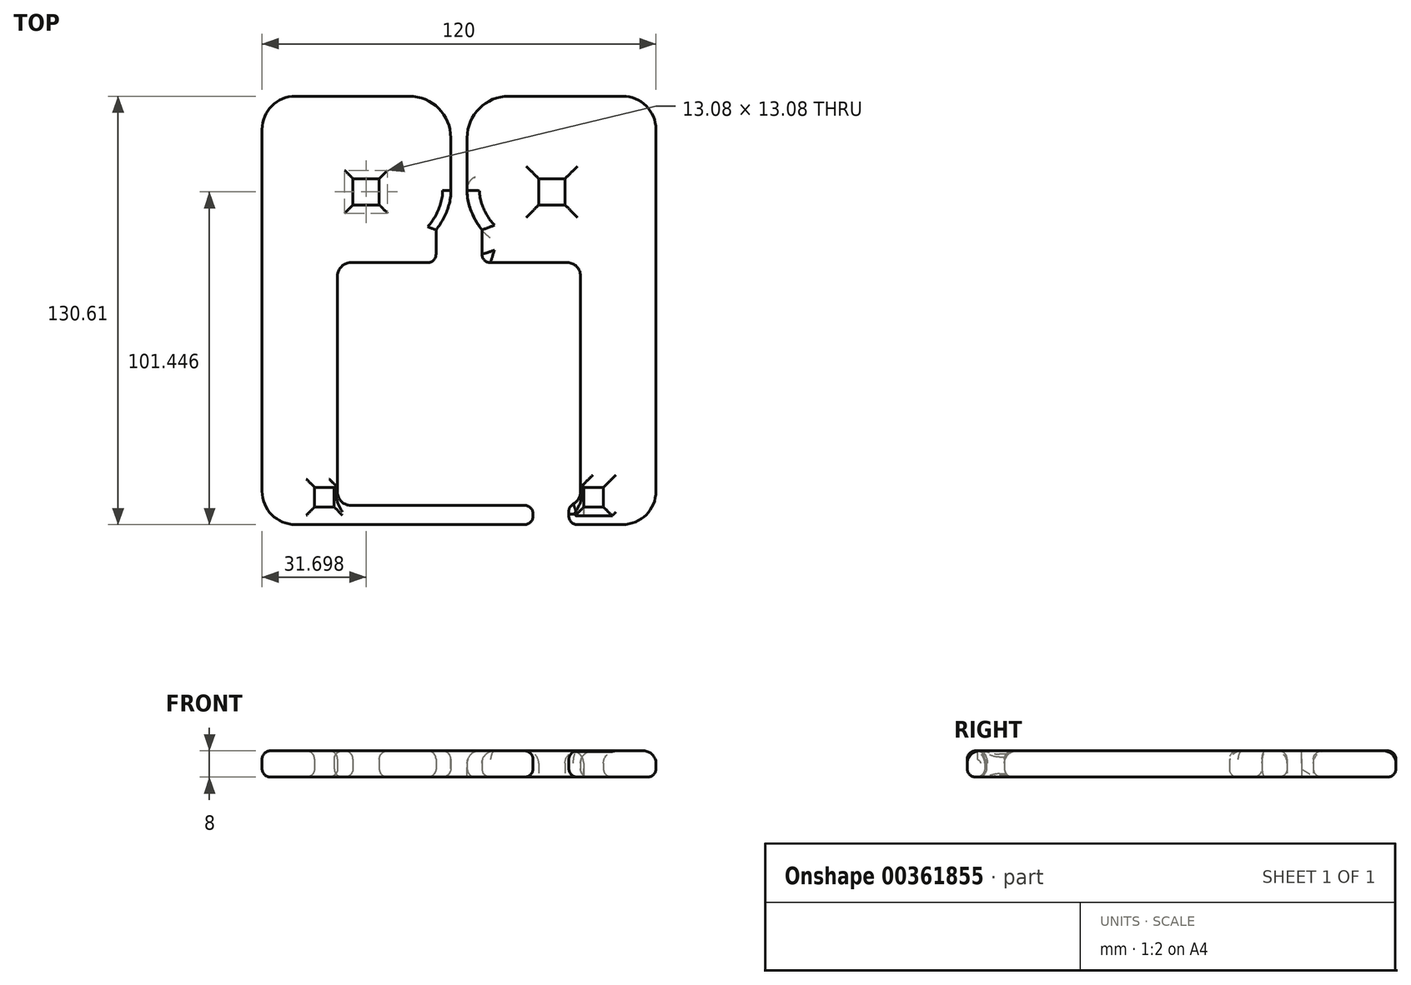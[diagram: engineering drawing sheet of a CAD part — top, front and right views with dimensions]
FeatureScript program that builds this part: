
annotation { "Feature Type Name" : "Feature", "Feature Type Description" : "" }
export const myFeature = defineFeature(function(context is Context, id is Id, definition is map)
    precondition{}
    {
        {
            var Q0;
            Q0=qCreatedBy(makeId("Top.planeOp"),FACE);
            var sketch = newSketch(context, id + "F0", { "sketchPlane" : qUnion([Q0])});
            skLineSegment(sketch, "E0.2", {"start": v(-99.34, -42.29) * mm, "end": v(-99.34, 23.71) * mm});
            skArc(sketch, "E0.3", {"start": v(-112.18, 78.48) * mm, "mid": v(-119.37, 75.5) * mm, "end": v(-122.34, 68.32) * mm});
            skLineSegment(sketch, "E0.5", {"start": v(-95.34, 23.71) * mm, "end": v(-99.34, 23.71) * mm});
            skLineSegment(sketch, "E1.0.0", {"start": v(-122.34, 68.32) * mm, "end": v(-122.34, -41.97) * mm});
            skLineSegment(sketch, "E1.0.4", {"start": v(-2.34, -41.97) * mm, "end": v(-2.34, 68.32) * mm});
            skArc(sketch, "E1.0.5", {"start": v(-2.34, 68.32) * mm, "mid": v(-5.32, 75.5) * mm, "end": v(-12.5, 78.48) * mm});
            skLineSegment(sketch, "E1.0.6", {"start": v(-12.5, 78.48) * mm, "end": v(-47.14, 78.48) * mm});
            skLineSegment(sketch, "E2.0.0", {"start": v(-28.87, -46.26) * mm, "end": v(-28.87, -52.13) * mm});
            skLineSegment(sketch, "E2.0.11", {"start": v(-39.8, -52.13) * mm, "end": v(-39.8, -46.29) * mm});
            skLineSegment(sketch, "E2.0.12", {"start": v(-39.8, -46.29) * mm, "end": v(-95.34, -46.29) * mm});
            skArc(sketch, "E2.0.13", {"start": v(-95.34, -46.29) * mm, "mid": v(-98.17, -45.12) * mm, "end": v(-99.34, -42.29) * mm});
            skArc(sketch, "E2.0.15", {"start": v(-99.34, 23.71) * mm, "mid": v(-98.17, 26.54) * mm, "end": v(-95.34, 27.71) * mm});
            skLineSegment(sketch, "E2.0.16", {"start": v(-95.34, 27.71) * mm, "end": v(-69.34, 27.71) * mm});
            skArc(sketch, "E2.0.17", {"start": v(-29.34, 27.71) * mm, "mid": v(-26.51, 26.54) * mm, "end": v(-25.34, 23.71) * mm});
            skLineSegment(sketch, "E2.0.18", {"start": v(-25.34, 23.71) * mm, "end": v(-25.34, -42.29) * mm});
            skArc(sketch, "E2.0.19", {"start": v(-25.34, -42.29) * mm, "mid": v(-26.35, -44.95) * mm, "end": v(-28.87, -46.26) * mm});
            skLineSegment(sketch, "E3.0.0", {"start": v(-94.64, 53.32) * mm, "end": v(-94.64, 45.32) * mm});
            skLineSegment(sketch, "E3.0.1", {"start": v(-94.64, 45.32) * mm, "end": v(-86.64, 45.32) * mm});
            skLineSegment(sketch, "E3.0.2", {"start": v(-86.64, 45.32) * mm, "end": v(-86.64, 53.32) * mm});
            skLineSegment(sketch, "E3.0.3", {"start": v(-86.64, 53.32) * mm, "end": v(-94.64, 53.32) * mm});
            skLineSegment(sketch, "E4.0.0", {"start": v(-30.04, 45.32) * mm, "end": v(-30.04, 53.32) * mm});
            skLineSegment(sketch, "E4.0.1", {"start": v(-30.04, 53.32) * mm, "end": v(-38.04, 53.32) * mm});
            skLineSegment(sketch, "E4.0.2", {"start": v(-38.04, 53.32) * mm, "end": v(-38.04, 45.32) * mm});
            skLineSegment(sketch, "E4.0.3", {"start": v(-38.04, 45.32) * mm, "end": v(-30.04, 45.32) * mm});
            skLineSegment(sketch, "E5", {"start": v(-105.84, -43.79) * mm, "end": v(-106.34, -43.79) * mm, "construction": true});
            skLineSegment(sketch, "E6", {"start": v(-103.34, -41.29) * mm, "end": v(-103.34, -40.79) * mm, "construction": true});
            skLineSegment(sketch, "E7.bottom", {"start": v(-106.34, -40.79) * mm, "end": v(-100.34, -40.79) * mm});
            skLineSegment(sketch, "E7.top", {"start": v(-106.34, -46.79) * mm, "end": v(-100.34, -46.79) * mm});
            skLineSegment(sketch, "E7.left", {"start": v(-106.34, -40.79) * mm, "end": v(-106.34, -46.79) * mm});
            skLineSegment(sketch, "E7.right", {"start": v(-100.34, -40.79) * mm, "end": v(-100.34, -46.79) * mm});
            skLineSegment(sketch, "E8", {"start": v(-99.34, -9.29) * mm, "end": v(-25.34, -9.29) * mm, "construction": true});
            skLineSegment(sketch, "E9", {"start": v(-62.34, -3.3) * mm, "end": v(-62.34, -18.16) * mm, "construction": true});
            skPoint(sketch, "E9.startSnap0", {"position": v(-62.34, -9.29) * mm});
            skLineSegment(sketch, "E10.MirrorCS", {"start": v(-21.34, -41.29) * mm, "end": v(-21.34, -40.79) * mm, "construction": true});
            skLineSegment(sketch, "E11.MirrorCS", {"start": v(-24.34, -40.79) * mm, "end": v(-24.34, -46.79) * mm});
            skLineSegment(sketch, "E12.MirrorCS", {"start": v(-18.34, -40.79) * mm, "end": v(-18.34, -46.79) * mm});
            skLineSegment(sketch, "E13.MirrorCS", {"start": v(-18.34, -40.79) * mm, "end": v(-24.34, -40.79) * mm});
            skLineSegment(sketch, "E14.MirrorCS", {"start": v(-18.34, -46.79) * mm, "end": v(-24.34, -46.79) * mm});
            skLineSegment(sketch, "E15", {"start": v(-99.34, -3.05) * mm, "end": v(-69.34, -3.05) * mm, "construction": true});
            skLineSegment(sketch, "E16", {"start": v(-25.34, -3.05) * mm, "end": v(-55.34, -3.05) * mm, "construction": true});
            skLineSegment(sketch, "E17", {"start": v(-69.34, -3.05) * mm, "end": v(-69.34, 27.71) * mm, "construction": true});
            skLineSegment(sketch, "E18", {"start": v(-55.34, 27.71) * mm, "end": v(-55.34, -3.05) * mm, "construction": true});
            skLineSegment(sketch, "E19.trimOffspring", {"start": v(-55.34, 27.71) * mm, "end": v(-29.34, 27.71) * mm});
            skLineSegment(sketch, "E20", {"start": v(-69.34, 27.71) * mm, "end": v(-69.34, 37.71) * mm});
            skLineSegment(sketch, "E21", {"start": v(-55.34, 27.71) * mm, "end": v(-55.34, 37.71) * mm});
            skLineSegment(sketch, "E22", {"start": v(-64.84, 48.63) * mm, "end": v(-64.84, 65.78) * mm});
            skLineSegment(sketch, "E23", {"start": v(-59.84, 48.63) * mm, "end": v(-59.84, 65.78) * mm});
            skEllipticalArc(sketch, "E24", {});
            skEllipticalArc(sketch, "E25.MirrorC", {});
            skLineSegment(sketch, "E26.trimOffspring", {"start": v(-77.54, 78.48) * mm, "end": v(-112.18, 78.48) * mm});
            skPoint(sketch, "E27.visualSharp", {"position": v(-64.84, 78.48) * mm});
            skArc(sketch, "E27.filletArc", {"start": v(-64.84, 65.78) * mm, "mid": v(-68.56, 74.76) * mm, "end": v(-77.54, 78.48) * mm});
            skPoint(sketch, "E28.visualSharp", {"position": v(-59.84, 78.48) * mm});
            skArc(sketch, "E28.filletArc", {"start": v(-47.14, 78.48) * mm, "mid": v(-56.12, 74.76) * mm, "end": v(-59.84, 65.78) * mm});
            skLineSegment(sketch, "E29", {"start": v(-112.18, -52.13) * mm, "end": v(-39.8, -52.13) * mm});
            skPoint(sketch, "E30.visualSharp", {"position": v(-2.34, -52.13) * mm});
            skArc(sketch, "E30.filletArc", {"start": v(-12.5, -52.13) * mm, "mid": v(-5.32, -49.16) * mm, "end": v(-2.34, -41.97) * mm});
            skPoint(sketch, "E31.visualSharp", {"position": v(-122.34, -52.13) * mm});
            skArc(sketch, "E31.filletArc", {"start": v(-122.34, -41.97) * mm, "mid": v(-119.37, -49.16) * mm, "end": v(-112.18, -52.13) * mm});
            skLineSegment(sketch, "E32.trimOffspring", {"start": v(-28.87, -52.13) * mm, "end": v(-12.5, -52.13) * mm});
            const initialGuessF0  = {"E24": [-0.07160861045122147, 0.04385959729552269, -0.4506115327281223, -0.8927201389978903, 0.010858769683543398, 0.005259403551116595, 1.146709446237365, 2.4446029381637704], "E25.MirrorC": [-0.053077005265114885, 0.04385959729552269, 0.4506115327281223, -0.8927201389978903, 0.010858769683543398, 0.005259403551116595, 3.838582369015851, 5.1364758609422205]};
            skSetInitialGuess(sketch, initialGuessF0);
            skSolve(sketch);
        }
        {
            var Q0;
            Q0 = qSketchRegion(id + "F0", true);
            extrude(context, id + "F1", {"entities" : qUnion([Q0]), "depth" : 8 * mm});
        }
        {
            var Q0;
            Q0=makeQuery(id+"F1.opExtrude","SWEPT_EDGE",EDGE,{"disambiguationData":[OSD([sQuery(id+"F0.wireOp",EDGE,"E2.0.11"),sQuery(id+"F0.wireOp",EDGE,"E29")])]});
            var Q1;
            Q1=makeQuery(id+"F1.opExtrude","SWEPT_EDGE",EDGE,{"disambiguationData":[OSD([sQuery(id+"F0.wireOp",EDGE,"E2.0.11"),sQuery(id+"F0.wireOp",EDGE,"E2.0.12")])]});
            var Q2;
            Q2=makeQuery(id+"F1.opExtrude","SWEPT_EDGE",EDGE,{"disambiguationData":[OSD([sQuery(id+"F0.wireOp",EDGE,"E2.0.16"),sQuery(id+"F0.wireOp",EDGE,"E20")])]});
            var Q3;
            Q3=makeQuery(id+"F1.opExtrude","SWEPT_EDGE",EDGE,{"disambiguationData":[OSD([sQuery(id+"F0.wireOp",EDGE,"E19.trimOffspring"),sQuery(id+"F0.wireOp",EDGE,"E21")])]});
            fillet(context, id + "F2", {"entities" : qUnion([Q0, Q1, Q2, Q3]), "radius" : 2.54 * mm, "tangentPropagation" : true, "allowEdgeOverflow" : false});
        }
        {
            var Q0;
            Q0=makeQuery(id+"F1.opExtrude","CAP_EDGE",EDGE,{"disambiguationData":[OSD([sQuery(id+"F0.wireOp",EDGE,"E27.filletArc")])],"isStart":true});
            var Q1;
            Q1=makeQuery(id+"F1.opExtrude","CAP_FACE",FACE,{"disambiguationData":[OSD([sQuery(id+"F0.wireOp",EDGE,"E1.0.0"),sQuery(id+"F0.wireOp",EDGE,"E0.3"),sQuery(id+"F0.wireOp",EDGE,"E2.0.11"),sQuery(id+"F0.wireOp",EDGE,"E2.0.12"),sQuery(id+"F0.wireOp",EDGE,"E2.0.13"),sQuery(id+"F0.wireOp",EDGE,"E0.2"),sQuery(id+"F0.wireOp",EDGE,"E2.0.15"),sQuery(id+"F0.wireOp",EDGE,"E2.0.16"),sQuery(id+"F0.wireOp",EDGE,"E3.0.0"),sQuery(id+"F0.wireOp",EDGE,"E3.0.1"),sQuery(id+"F0.wireOp",EDGE,"E3.0.2"),sQuery(id+"F0.wireOp",EDGE,"E3.0.3"),sQuery(id+"F0.wireOp",EDGE,"E7.bottom"),sQuery(id+"F0.wireOp",EDGE,"E7.top"),sQuery(id+"F0.wireOp",EDGE,"E7.left"),sQuery(id+"F0.wireOp",EDGE,"E7.right"),sQuery(id+"F0.wireOp",EDGE,"E20"),sQuery(id+"F0.wireOp",EDGE,"E22"),sQuery(id+"F0.wireOp",EDGE,"E24"),sQuery(id+"F0.wireOp",EDGE,"E26.trimOffspring"),sQuery(id+"F0.wireOp",EDGE,"E27.filletArc"),sQuery(id+"F0.wireOp",EDGE,"E29"),sQuery(id+"F0.wireOp",EDGE,"E31.filletArc")])],"isStart":true});
            var Q2;
            Q2=makeQuery(id+"F1.opExtrude","CAP_FACE",FACE,{"disambiguationData":[OSD([sQuery(id+"F0.wireOp",EDGE,"E1.0.0"),sQuery(id+"F0.wireOp",EDGE,"E0.3"),sQuery(id+"F0.wireOp",EDGE,"E2.0.11"),sQuery(id+"F0.wireOp",EDGE,"E2.0.12"),sQuery(id+"F0.wireOp",EDGE,"E2.0.13"),sQuery(id+"F0.wireOp",EDGE,"E0.2"),sQuery(id+"F0.wireOp",EDGE,"E2.0.15"),sQuery(id+"F0.wireOp",EDGE,"E2.0.16"),sQuery(id+"F0.wireOp",EDGE,"E3.0.0"),sQuery(id+"F0.wireOp",EDGE,"E3.0.1"),sQuery(id+"F0.wireOp",EDGE,"E3.0.2"),sQuery(id+"F0.wireOp",EDGE,"E3.0.3"),sQuery(id+"F0.wireOp",EDGE,"E7.bottom"),sQuery(id+"F0.wireOp",EDGE,"E7.top"),sQuery(id+"F0.wireOp",EDGE,"E7.left"),sQuery(id+"F0.wireOp",EDGE,"E7.right"),sQuery(id+"F0.wireOp",EDGE,"E20"),sQuery(id+"F0.wireOp",EDGE,"E22"),sQuery(id+"F0.wireOp",EDGE,"E24"),sQuery(id+"F0.wireOp",EDGE,"E26.trimOffspring"),sQuery(id+"F0.wireOp",EDGE,"E27.filletArc"),sQuery(id+"F0.wireOp",EDGE,"E29"),sQuery(id+"F0.wireOp",EDGE,"E31.filletArc")])],"isStart":false});
            fillet(context, id + "F3", {"entities" : qUnion([Q0, Q1, Q2]), "radius" : 2.54 * mm, "tangentPropagation" : true, "allowEdgeOverflow" : false});
        }
        {
            var Q0;
            Q0=makeQuery(id+"F1.opExtrude","CAP_FACE",FACE,{"disambiguationData":[OSD([sQuery(id+"F0.wireOp",EDGE,"E1.0.4"),sQuery(id+"F0.wireOp",EDGE,"E1.0.5"),sQuery(id+"F0.wireOp",EDGE,"E1.0.6"),sQuery(id+"F0.wireOp",EDGE,"E2.0.0"),sQuery(id+"F0.wireOp",EDGE,"E2.0.17"),sQuery(id+"F0.wireOp",EDGE,"E2.0.18"),sQuery(id+"F0.wireOp",EDGE,"E2.0.19"),sQuery(id+"F0.wireOp",EDGE,"E4.0.0"),sQuery(id+"F0.wireOp",EDGE,"E4.0.1"),sQuery(id+"F0.wireOp",EDGE,"E4.0.2"),sQuery(id+"F0.wireOp",EDGE,"E4.0.3"),sQuery(id+"F0.wireOp",EDGE,"E11.MirrorCS"),sQuery(id+"F0.wireOp",EDGE,"E12.MirrorCS"),sQuery(id+"F0.wireOp",EDGE,"E13.MirrorCS"),sQuery(id+"F0.wireOp",EDGE,"E14.MirrorCS"),sQuery(id+"F0.wireOp",EDGE,"E19.trimOffspring"),sQuery(id+"F0.wireOp",EDGE,"E21"),sQuery(id+"F0.wireOp",EDGE,"E23"),sQuery(id+"F0.wireOp",EDGE,"E25.MirrorC"),sQuery(id+"F0.wireOp",EDGE,"E28.filletArc"),sQuery(id+"F0.wireOp",EDGE,"E30.filletArc"),sQuery(id+"F0.wireOp",EDGE,"E32.trimOffspring")])],"isStart":false});
            fillet(context, id + "F4", {"entities" : qUnion([Q0]), "radius" : 3.8 * mm, "tangentPropagation" : true, "allowEdgeOverflow" : false});
        }
        {
            var Q0;
            Q0=makeQuery(id+"F1.opExtrude","SWEPT_EDGE",EDGE,{"disambiguationData":[OSD([sQuery(id+"F0.wireOp",EDGE,"E2.0.0"),sQuery(id+"F0.wireOp",EDGE,"E32.trimOffspring")])]});
            var Q1;
            Q1=makeQuery(id+"F1.opExtrude","SWEPT_EDGE",EDGE,{"disambiguationData":[OSD([sQuery(id+"F0.wireOp",EDGE,"E2.0.0"),sQuery(id+"F0.wireOp",EDGE,"E2.0.19")])]});
            fillet(context, id + "F5", {"entities" : qUnion([Q0, Q1]), "radius" : 2.54 * mm, "tangentPropagation" : true, "allowEdgeOverflow" : false});
        }
        {
            var Q0;
            Q0=makeQuery(id+"F1.opExtrude","CAP_EDGE",EDGE,{"disambiguationData":[OSD([sQuery(id+"F0.wireOp",EDGE,"E1.0.4")])],"isStart":true});
            var Q1;
            Q1=makeQuery(id+"F1.opExtrude","CAP_EDGE",EDGE,{"disambiguationData":[OSD([sQuery(id+"F0.wireOp",EDGE,"E2.0.18")])],"isStart":true});
            var Q2;
            Q2=makeQuery(id+"F1.opExtrude","CAP_EDGE",EDGE,{"disambiguationData":[OSD([sQuery(id+"F0.wireOp",EDGE,"E2.0.17")])],"isStart":true});
            var Q3;
            Q3=makeQuery(id+"F1.opExtrude","CAP_EDGE",EDGE,{"disambiguationData":[OSD([sQuery(id+"F0.wireOp",EDGE,"E14.MirrorCS")])],"isStart":true});
            var Q4;
            Q4=makeQuery(id+"F1.opExtrude","CAP_EDGE",EDGE,{"disambiguationData":[OSD([sQuery(id+"F0.wireOp",EDGE,"E12.MirrorCS")])],"isStart":true});
            var Q5;
            Q5=makeQuery(id+"F1.opExtrude","CAP_EDGE",EDGE,{"disambiguationData":[OSD([sQuery(id+"F0.wireOp",EDGE,"E13.MirrorCS")])],"isStart":true});
            fillet(context, id + "F6", {"entities" : qUnion([Q0, Q1, Q2, Q3, Q4, Q5]), "radius" : 2.54 * mm, "tangentPropagation" : true, "allowEdgeOverflow" : false});
        }
    });
